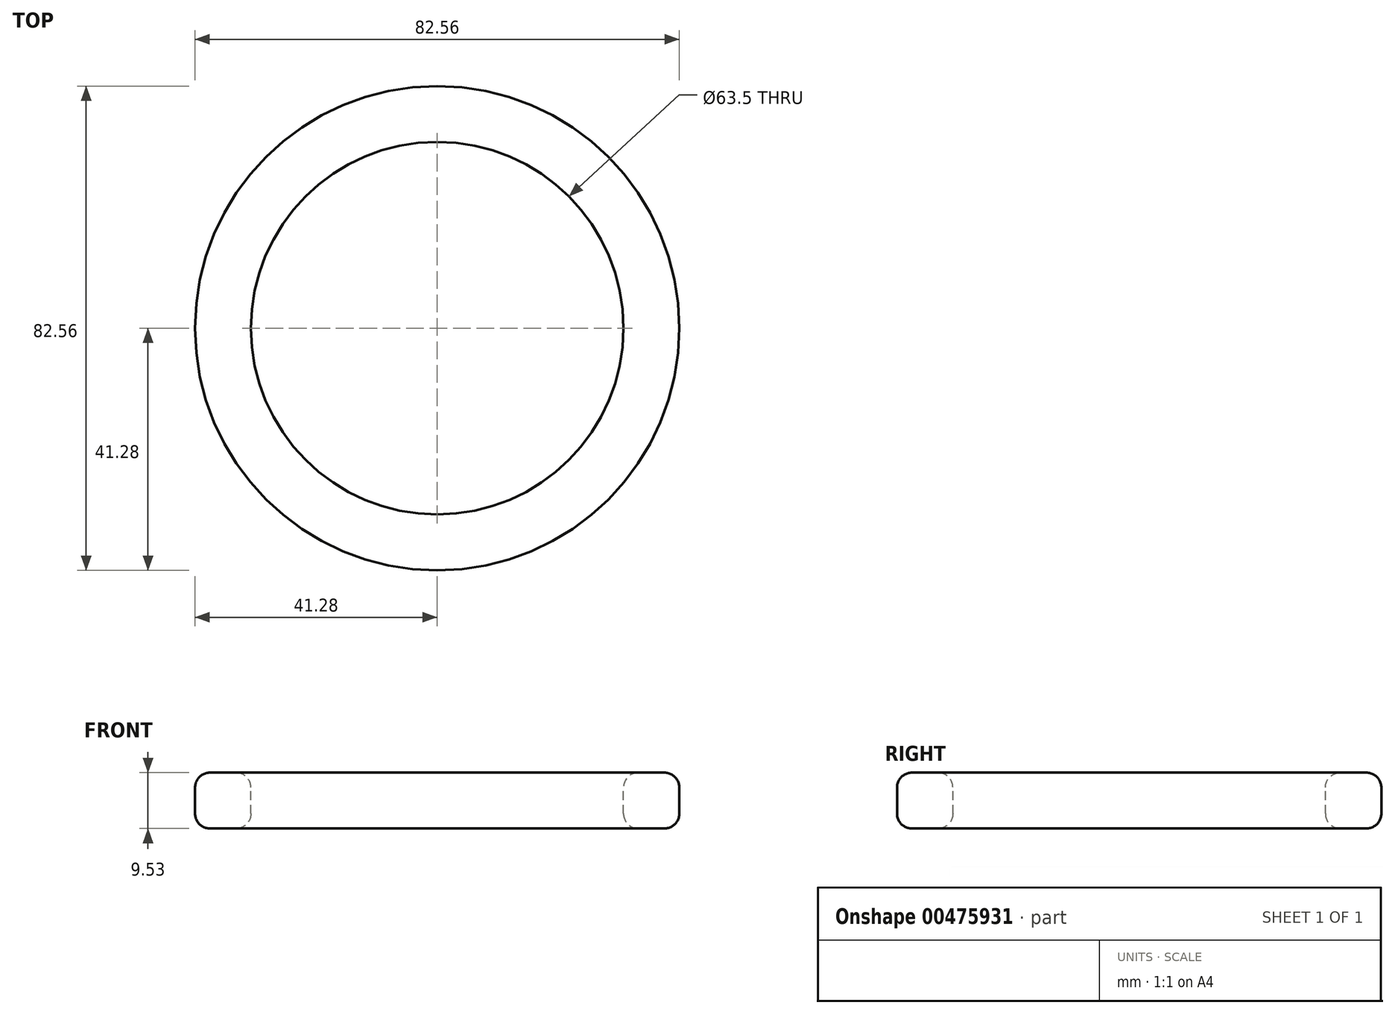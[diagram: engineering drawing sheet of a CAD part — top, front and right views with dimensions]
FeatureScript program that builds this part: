
annotation { "Feature Type Name" : "Feature", "Feature Type Description" : "" }
export const myFeature = defineFeature(function(context is Context, id is Id, definition is map)
    precondition{}
    {
        {
            var Q0;
            Q0=qCreatedBy(makeId("Front.planeOp"),FACE);
            var sketch = newSketch(context, id + "F0", { "sketchPlane" : qUnion([Q0])});
            skLineSegment(sketch, "E0.bottom", {"start": v(31.75, 5.04) * mm, "end": v(41.27, 5.04) * mm});
            skLineSegment(sketch, "E0.top", {"start": v(31.75, -4.49) * mm, "end": v(41.27, -4.49) * mm});
            skLineSegment(sketch, "E0.left", {"start": v(31.75, 5.04) * mm, "end": v(31.75, -4.49) * mm});
            skLineSegment(sketch, "E0.right", {"start": v(41.27, 5.04) * mm, "end": v(41.27, -4.49) * mm});
            skLineSegment(sketch, "E1", {"start": v(0, 20.45) * mm, "end": v(0, -20.73) * mm});
            skSolve(sketch);
        }
        {
            var Q0;
            Q0=makeQuery(id+"F0.imprint","IMPRINT",FACE,{"disambiguationData":[TD([[makeQuery(id+"F0.imprint","IMPRINT",EDGE,{"derivedFrom":sQuery(id+"F0.wireOp",EDGE,"E0.bottom")}),-1.0]])]});
            var Q1;
            Q1=sQuery(id+"F0.wireOp",EDGE,"E1");
            revolve(context, id + "F1", {"entities" : qUnion([Q0]), "axis" : qUnion([Q1]), "revolveType" : RevolveType.FULL});
        }
        {
            var Q0;
            Q0=makeQuery(id+"F1.opRevolve","SWEPT_EDGE",EDGE,{"disambiguationData":[OSD([sQuery(id+"F0.wireOp",EDGE,"E0.bottom"),sQuery(id+"F0.wireOp",EDGE,"E0.right")])]});
            var Q1;
            Q1=makeQuery(id+"F1.opRevolve","SWEPT_EDGE",EDGE,{"disambiguationData":[OSD([sQuery(id+"F0.wireOp",EDGE,"E0.bottom"),sQuery(id+"F0.wireOp",EDGE,"E0.left")])]});
            var Q2;
            Q2=makeQuery(id+"F1.opRevolve","SWEPT_EDGE",EDGE,{"disambiguationData":[OSD([sQuery(id+"F0.wireOp",EDGE,"E0.top"),sQuery(id+"F0.wireOp",EDGE,"E0.right")])]});
            var Q3;
            Q3=makeQuery(id+"F1.opRevolve","SWEPT_EDGE",EDGE,{"disambiguationData":[OSD([sQuery(id+"F0.wireOp",EDGE,"E0.top"),sQuery(id+"F0.wireOp",EDGE,"E0.left")])]});
            fillet(context, id + "F2", {"entities" : qUnion([Q0, Q1, Q2, Q3]), "radius" : 2.54 * mm, "tangentPropagation" : true, "allowEdgeOverflow" : false});
        }
    });
